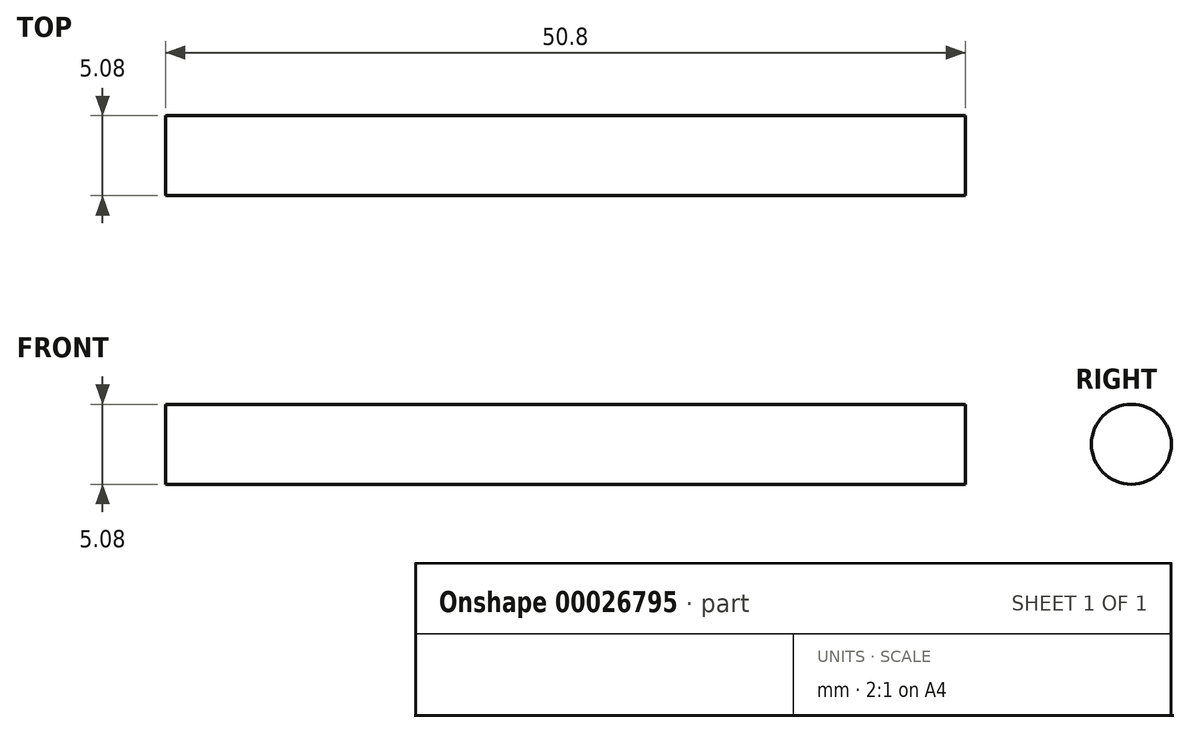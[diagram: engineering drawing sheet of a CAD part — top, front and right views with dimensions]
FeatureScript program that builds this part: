
annotation { "Feature Type Name" : "Feature", "Feature Type Description" : "" }
export const myFeature = defineFeature(function(context is Context, id is Id, definition is map)
    precondition{}
    {
        {
            var Q0;
            Q0=qCreatedBy(makeId("Top.planeOp"),FACE);
            var sketch = newSketch(context, id + "F0", { "sketchPlane" : qUnion([Q0])});
            skLineSegment(sketch, "E0.bottom", {"start": v(-38.27, 2.54) * mm, "end": v(12.53, 2.54) * mm});
            skLineSegment(sketch, "E0.top", {"start": v(-38.27, 0) * mm, "end": v(12.53, 0) * mm});
            skLineSegment(sketch, "E0.left", {"start": v(-38.27, 2.54) * mm, "end": v(-38.27, 0) * mm});
            skLineSegment(sketch, "E0.right", {"start": v(12.53, 2.54) * mm, "end": v(12.53, 0) * mm});
            skSolve(sketch);
        }
        {
            var Q0;
            Q0=makeQuery(id+"F0.imprint","IMPRINT",FACE,{"disambiguationData":[TD([[makeQuery(id+"F0.imprint","IMPRINT",EDGE,{"derivedFrom":sQuery(id+"F0.wireOp",EDGE,"E0.bottom")}),-1.0]])]});
            var Q1;
            Q1=sQuery(id+"F0.wireOp",EDGE,"E0.top");
            revolve(context, id + "F1", {"entities" : qUnion([Q0]), "axis" : qUnion([Q1]), "revolveType" : RevolveType.FULL});
        }
    });
